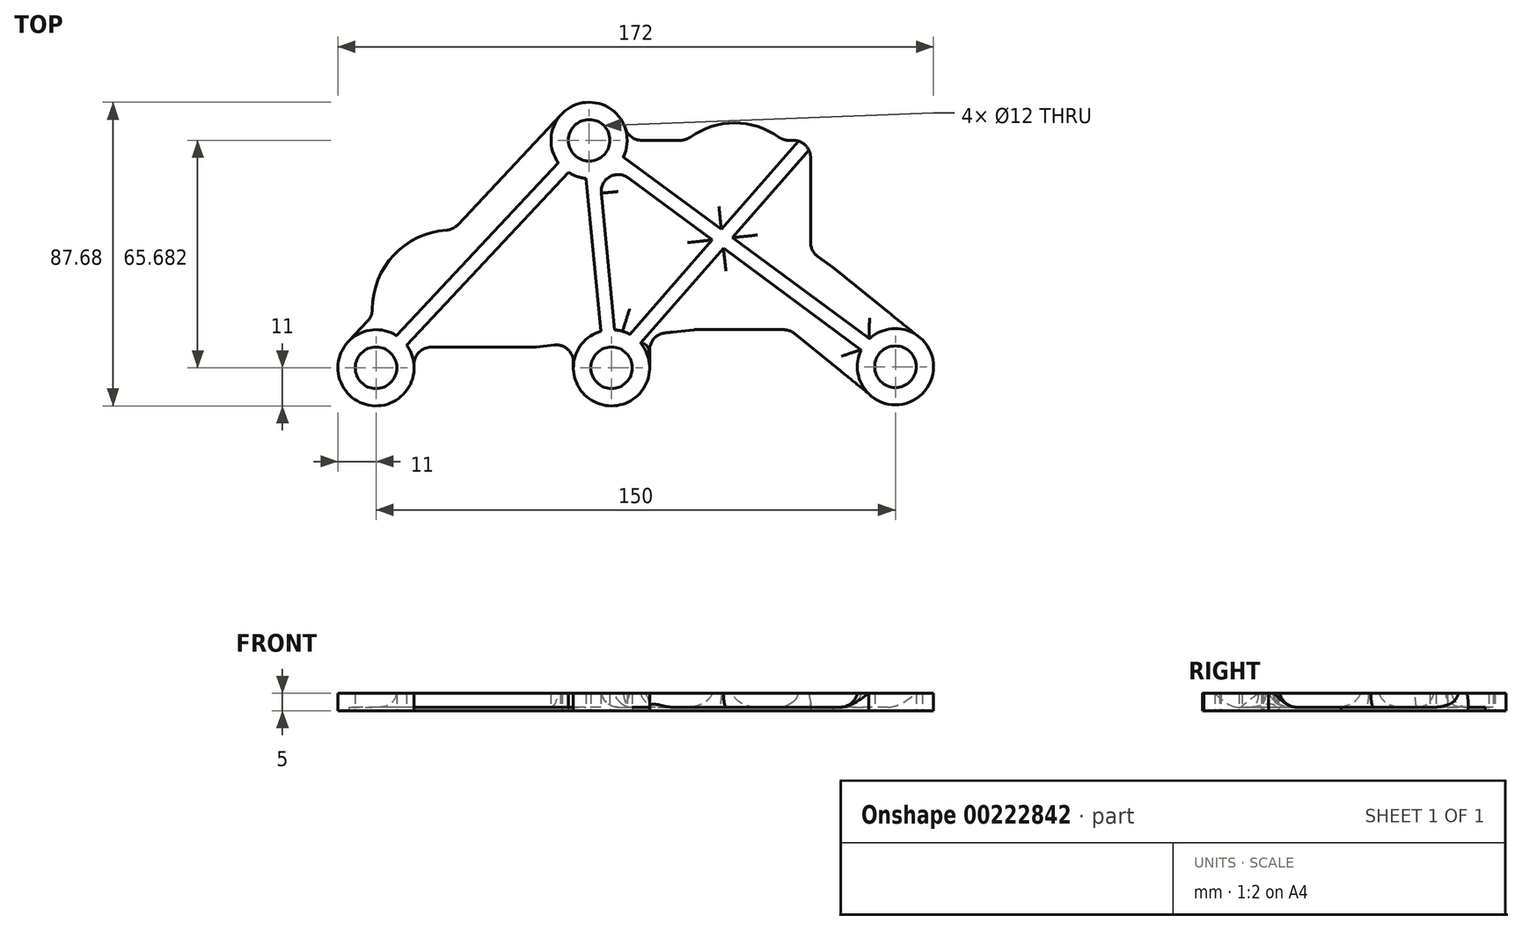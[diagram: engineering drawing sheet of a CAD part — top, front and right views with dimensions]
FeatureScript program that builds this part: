
annotation { "Feature Type Name" : "Feature", "Feature Type Description" : "" }
export const myFeature = defineFeature(function(context is Context, id is Id, definition is map)
    precondition{}
    {
        {
            var Q0;
            Q0=qCreatedBy(makeId("Top.planeOp"),FACE);
            var sketch = newSketch(context, id + "F0", { "sketchPlane" : qUnion([Q0])});
            skCircle(sketch, "E0", {"center": v(0, 0) * mm, "radius": 6 * mm});
            skCircle(sketch, "E1", {"center": v(-68, 0) * mm, "radius": 6 * mm});
            skCircle(sketch, "E2", {"center": v(-6.47, 65.68) * mm, "radius": 6 * mm});
            skArc(sketch, "E3", {"start": v(-75.78, 7.78) * mm, "mid": v(-72, -10.24) * mm, "end": v(-57, 0.43) * mm});
            skArc(sketch, "E4", {"start": v(-11, 0) * mm, "mid": v(0, -11) * mm, "end": v(11, 0) * mm});
            skArc(sketch, "E5", {"start": v(-14.25, 73.46) * mm, "mid": v(-14.5, 73.2) * mm, "end": v(-14.74, 72.94) * mm});
            skLineSegment(sketch, "E6", {"start": v(-68, 0) * mm, "end": v(-68, -11) * mm, "construction": true});
            skLineSegment(sketch, "E7", {"start": v(0, 0) * mm, "end": v(0, -11) * mm, "construction": true});
            skLineSegment(sketch, "E8", {"start": v(0, -11) * mm, "end": v(-68, -11) * mm, "construction": true});
            skLineSegment(sketch, "E9", {"start": v(0, -11) * mm, "end": v(48, -11) * mm, "construction": true});
            skLineSegment(sketch, "E10", {"start": v(48, -11) * mm, "end": v(-22, -11) * mm, "construction": true});
            skLineSegment(sketch, "E11", {"start": v(-22, -11) * mm, "end": v(-22, 6) * mm, "construction": true});
            skLineSegment(sketch, "E12", {"start": v(24, -11) * mm, "end": v(24, 11) * mm, "construction": true});
            skLineSegment(sketch, "E13", {"start": v(24.27, 11) * mm, "end": v(49.68, 11) * mm});
            skLineSegment(sketch, "E14", {"start": v(-6.47, 65.68) * mm, "end": v(1.3, 73.46) * mm, "construction": true});
            skLineSegment(sketch, "E15", {"start": v(-11, 0) * mm, "end": v(11, 0) * mm, "construction": true});
            skLineSegment(sketch, "E16", {"start": v(23.73, 10.97) * mm, "end": v(15.46, 10.07) * mm});
            skLineSegment(sketch, "E17.trimOffspring", {"start": v(-16.54, 6.6) * mm, "end": v(-21.73, 6.03) * mm});
            skLineSegment(sketch, "E18", {"start": v(-6.47, 65.68) * mm, "end": v(-14.25, 73.46) * mm, "construction": true});
            skLineSegment(sketch, "E19", {"start": v(-68, 0) * mm, "end": v(-75.78, 7.78) * mm, "construction": true});
            skLineSegment(sketch, "E20", {"start": v(-68, 0) * mm, "end": v(-79, 0) * mm, "construction": true});
            skLineSegment(sketch, "E21", {"start": v(-75.78, 7.78) * mm, "end": v(-70.43, 13.48) * mm});
            skLineSegment(sketch, "E22", {"start": v(-57, -0.43) * mm, "end": v(-57, 1) * mm});
            skLineSegment(sketch, "E23", {"start": v(-22.27, 6) * mm, "end": v(-52, 6) * mm});
            skPoint(sketch, "E24.orphan", {"position": v(-57, 12.43) * mm});
            skLineSegment(sketch, "E25", {"start": v(11, 0) * mm, "end": v(11, 5.1) * mm});
            skLineSegment(sketch, "E26", {"start": v(-11, 0) * mm, "end": v(-11, 1.62) * mm});
            skPoint(sketch, "E27", {"position": v(-69.01, 15) * mm});
            skPoint(sketch, "E28", {"position": v(-45.77, 39.81) * mm});
            skLineSegment(sketch, "E29", {"start": v(-62.63, 32.79) * mm, "end": v(-57.15, 27.66) * mm});
            skArc(sketch, "E30", {"start": v(-47.65, 39.76) * mm, "mid": v(-62.87, 32.54) * mm, "end": v(-69.08, 16.88) * mm});
            skPoint(sketch, "E31", {"position": v(52.5, 37.16) * mm});
            skPoint(sketch, "E32", {"position": v(25.66, 56.19) * mm});
            skLineSegment(sketch, "E33", {"start": v(52.8, 73.14) * mm, "end": v(52.5, 73.16) * mm});
            skLineSegment(sketch, "E34.trimOffspring", {"start": v(59.6, 32.11) * mm, "end": v(64, 29) * mm});
            skPoint(sketch, "E35", {"position": v(82, 0.31) * mm});
            skCircle(sketch, "E36", {"center": v(82, 0.31) * mm, "radius": 6 * mm});
            skArc(sketch, "E37", {"start": v(74.22, -7.46) * mm, "mid": v(90.54, -6.61) * mm, "end": v(88, 9.53) * mm});
            skLineSegment(sketch, "E38", {"start": v(82, 0.31) * mm, "end": v(93, 0.31) * mm, "construction": true});
            skLineSegment(sketch, "E39", {"start": v(93, 0.31) * mm, "end": v(82, 0.31) * mm, "construction": true});
            skLineSegment(sketch, "E40", {"start": v(82, 0.31) * mm, "end": v(89.78, 8.1) * mm, "construction": true});
            skLineSegment(sketch, "E41", {"start": v(89.78, 8.1) * mm, "end": v(64, 29) * mm});
            skLineSegment(sketch, "E42", {"start": v(74.22, -7.46) * mm, "end": v(82, 0.31) * mm, "construction": true});
            skLineSegment(sketch, "E43", {"start": v(74.22, -7.46) * mm, "end": v(52.83, 9.88) * mm});
            skLineSegment(sketch, "E44.trimOffspring", {"start": v(-44.35, 41.33) * mm, "end": v(-14.25, 73.46) * mm});
            skPoint(sketch, "E45.visualSharp", {"position": v(-57, 6) * mm});
            skArc(sketch, "E45.filletArc", {"start": v(-52, 6) * mm, "mid": v(-55.54, 4.54) * mm, "end": v(-57, 1) * mm});
            skPoint(sketch, "E46.visualSharp", {"position": v(-22, 6) * mm});
            skArc(sketch, "E46.filletArc", {"start": v(-22.27, 6) * mm, "mid": v(-22, 6) * mm, "end": v(-21.73, 6.03) * mm});
            skArc(sketch, "E47.filletArc", {"start": v(-70.43, 13.48) * mm, "mid": v(-69.44, 15.05) * mm, "end": v(-69.08, 16.88) * mm});
            skArc(sketch, "E48.filletArc", {"start": v(-47.65, 39.76) * mm, "mid": v(-45.85, 40.23) * mm, "end": v(-44.35, 41.33) * mm});
            skPoint(sketch, "E49.visualSharp", {"position": v(-11, 7.2) * mm});
            skArc(sketch, "E49.filletArc", {"start": v(-11, 1.62) * mm, "mid": v(-12.66, 5.34) * mm, "end": v(-16.54, 6.6) * mm});
            skPoint(sketch, "E50.visualSharp", {"position": v(11, 9.59) * mm});
            skArc(sketch, "E50.filletArc", {"start": v(15.46, 10.07) * mm, "mid": v(12.28, 8.44) * mm, "end": v(11, 5.1) * mm});
            skPoint(sketch, "E51.visualSharp", {"position": v(24, 11) * mm});
            skArc(sketch, "E51.filletArc", {"start": v(24.27, 11) * mm, "mid": v(24, 11) * mm, "end": v(23.73, 10.97) * mm});
            skPoint(sketch, "E52.visualSharp", {"position": v(51.46, 11) * mm});
            skArc(sketch, "E52.filletArc", {"start": v(52.83, 9.88) * mm, "mid": v(51.35, 10.71) * mm, "end": v(49.68, 11) * mm});
            skPoint(sketch, "E53.visualSharp", {"position": v(52.5, 73.16) * mm});
            skLineSegment(sketch, "E54", {"start": v(57.5, 60.68) * mm, "end": v(57.5, 36.2) * mm});
            skPoint(sketch, "E55.visualSharp", {"position": v(57.5, 33.6) * mm});
            skArc(sketch, "E55.filletArc", {"start": v(57.5, 36.2) * mm, "mid": v(58.06, 33.9) * mm, "end": v(59.6, 32.11) * mm});
            skLineSegment(sketch, "E56.trimOffspring", {"start": v(4.53, 65.68) * mm, "end": v(12.3, 65.68) * mm, "construction": true});
            skLineSegment(sketch, "E57.trimOffspring", {"start": v(8.73, 65.68) * mm, "end": v(19.85, 65.68) * mm});
            skLineSegment(sketch, "E58", {"start": v(-68, 0) * mm, "end": v(-63.9, 4.38) * mm, "construction": true});
            skLineSegment(sketch, "E59.trimOffspring", {"start": v(-14, 57.65) * mm, "end": v(-6.47, 65.68) * mm, "construction": true});
            skArc(sketch, "E60.trimOffspring", {"start": v(3.98, 69.12) * mm, "mid": v(-4.27, 76.46) * mm, "end": v(-14.74, 72.94) * mm});
            skPoint(sketch, "E61.visualSharp", {"position": v(57.5, 65.68) * mm});
            skArc(sketch, "E61.filletArc", {"start": v(57.5, 60.68) * mm, "mid": v(56.04, 64.22) * mm, "end": v(52.5, 65.68) * mm});
            skPoint(sketch, "E62", {"position": v(21.53, 65.68) * mm});
            skPoint(sketch, "E63", {"position": v(49.53, 65.68) * mm});
            skPoint(sketch, "E64", {"position": v(35.53, 65.68) * mm});
            skArc(sketch, "E65", {"start": v(48.32, 66.6) * mm, "mid": v(35.53, 70.68) * mm, "end": v(22.74, 66.6) * mm});
            skLineSegment(sketch, "E66.trimOffspring", {"start": v(51.21, 65.68) * mm, "end": v(52.5, 65.68) * mm});
            skPoint(sketch, "E67.start.orphan", {"position": v(35.53, 70.68) * mm});
            skPoint(sketch, "E68.visualSharp", {"position": v(4.53, 65.68) * mm});
            skArc(sketch, "E68.filletArc", {"start": v(3.98, 69.12) * mm, "mid": v(5.8, 66.63) * mm, "end": v(8.73, 65.68) * mm});
            skArc(sketch, "E69.filletArc", {"start": v(19.85, 65.68) * mm, "mid": v(21.36, 65.92) * mm, "end": v(22.74, 66.6) * mm});
            skArc(sketch, "E70.filletArc", {"start": v(48.32, 66.6) * mm, "mid": v(49.7, 65.92) * mm, "end": v(51.21, 65.68) * mm});
            skSolve(sketch);
        }
        {
            var Q0;
            Q0=makeQuery(id+"F0.imprint","IMPRINT",FACE,{"disambiguationData":[TD([[makeQuery(id+"F0.imprint","IMPRINT",EDGE,{"derivedFrom":sQuery(id+"F0.wireOp",EDGE,"E13")}),1.0]])]});
            extrude(context, id + "F1", {"entities" : qUnion([Q0]), "depth" : 1 * mm});
        }
        {
            var Q0;
            Q0=makeQuery(id+"F1.opExtrude","CAP_FACE",FACE,{"disambiguationData":[OSD([sQuery(id+"F0.wireOp",EDGE,"E0"),sQuery(id+"F0.wireOp",EDGE,"E1"),sQuery(id+"F0.wireOp",EDGE,"E2"),sQuery(id+"F0.wireOp",EDGE,"E3"),sQuery(id+"F0.wireOp",EDGE,"E4"),sQuery(id+"F0.wireOp",EDGE,"E5"),sQuery(id+"F0.wireOp",EDGE,"E13"),sQuery(id+"F0.wireOp",EDGE,"E16"),sQuery(id+"F0.wireOp",EDGE,"E17.trimOffspring"),sQuery(id+"F0.wireOp",EDGE,"E21"),sQuery(id+"F0.wireOp",EDGE,"E22"),sQuery(id+"F0.wireOp",EDGE,"E23"),sQuery(id+"F0.wireOp",EDGE,"E25"),sQuery(id+"F0.wireOp",EDGE,"E26"),sQuery(id+"F0.wireOp",EDGE,"E30"),sQuery(id+"F0.wireOp",EDGE,"3UzAlsw2-RzgX-fS7Z-g7R3-vtdSIq3O0E33"),sQuery(id+"F0.wireOp",EDGE,"E33"),sQuery(id+"F0.wireOp",EDGE,"E34.trimOffspring"),sQuery(id+"F0.wireOp",EDGE,"E36"),sQuery(id+"F0.wireOp",EDGE,"E37"),sQuery(id+"F0.wireOp",EDGE,"E41"),sQuery(id+"F0.wireOp",EDGE,"E43"),sQuery(id+"F0.wireOp",EDGE,"E44.trimOffspring")])],"isStart":false});
            var sketch = newSketch(context, id + "F2", { "sketchPlane" : qUnion([Q0])});
            skLineSegment(sketch, "E71", {"start": v(-5.81, 76.66) * mm, "end": v(-6.47, 65.68) * mm, "construction": true});
            skLineSegment(sketch, "E72", {"start": v(-5.4, 54.74) * mm, "end": v(-6.47, 65.68) * mm, "construction": true});
            skPoint(sketch, "E73.orphan", {"position": v(-68, 0) * mm});
            skLineSegment(sketch, "E74", {"start": v(-68, 0) * mm, "end": v(-27.66, 43.06) * mm, "construction": true});
            skArc(sketch, "E75", {"start": v(-62.06, 9.26) * mm, "mid": v(-75.52, -8.03) * mm, "end": v(-59.15, 6.53) * mm});
            skLineSegment(sketch, "E76", {"start": v(-12.4, 56.42) * mm, "end": v(-59.15, 6.53) * mm});
            skLineSegment(sketch, "E77", {"start": v(-62.06, 9.26) * mm, "end": v(-15.33, 59.16) * mm});
            skLineSegment(sketch, "E78", {"start": v(-57, 1) * mm, "end": v(-67.68, 11) * mm, "construction": true});
            skPoint(sketch, "E79", {"position": v(-46.8, 22.62) * mm});
            skPoint(sketch, "E80", {"position": v(-27.66, 43.06) * mm});
            skPoint(sketch, "E81.startDerivative.orphan", {"position": v(-72.76, 11) * mm});
            skLineSegment(sketch, "E82.trimOffspring", {"start": v(-14, 57.65) * mm, "end": v(-6.47, 65.68) * mm, "construction": true});
            skLineSegment(sketch, "E83", {"start": v(0.93, 10.96) * mm, "end": v(-3.42, 55.11) * mm});
            skLineSegment(sketch, "E84", {"start": v(-3.05, 10.57) * mm, "end": v(-7.4, 54.72) * mm});
            skLineSegment(sketch, "E85", {"start": v(-6.47, 65.68) * mm, "end": v(-5.1, 67.14) * mm, "construction": true});
            skPoint(sketch, "E86.orphan", {"position": v(83.19, 1.92) * mm});
            skPoint(sketch, "E87.orphan", {"position": v(51.14, 71.88) * mm});
            skCircle(sketch, "E88.converted", {"center": v(82, 0.31) * mm, "radius": 11 * mm});
            skArc(sketch, "E89", {"start": v(-12.4, 56.42) * mm, "mid": v(-10, 55.27) * mm, "end": v(-7.4, 54.72) * mm});
            skArc(sketch, "E90.trimOffspring", {"start": v(-3.42, 55.11) * mm, "mid": v(-2.93, 76.1) * mm, "end": v(-15.33, 59.16) * mm});
            skArc(sketch, "E91", {"start": v(5.28, 9.65) * mm, "mid": v(3.17, 10.53) * mm, "end": v(0.93, 10.96) * mm});
            skLineSegment(sketch, "E92", {"start": v(-6.47, 65.68) * mm, "end": v(82, 0.31) * mm, "construction": true});
            skLineSegment(sketch, "E93", {"start": v(72.11, 5.13) * mm, "end": v(32.31, 34.54) * mm});
            skLineSegment(sketch, "E94", {"start": v(74.49, 8.35) * mm, "end": v(34.95, 37.56) * mm});
            skLineSegment(sketch, "E95.trimOffspring", {"start": v(31.72, 39.95) * mm, "end": v(3.42, 60.86) * mm});
            skLineSegment(sketch, "E96.trimOffspring", {"start": v(29.08, 36.93) * mm, "end": v(1.04, 57.65) * mm});
            skPoint(sketch, "E97.end.orphan", {"position": v(30.24, 38.56) * mm});
            skLineSegment(sketch, "E98", {"start": v(8.39, 7.12) * mm, "end": v(32.31, 34.54) * mm});
            skLineSegment(sketch, "E99", {"start": v(5.28, 9.65) * mm, "end": v(29.08, 36.93) * mm});
            skArc(sketch, "E100.trimOffspring", {"start": v(-3.05, 10.57) * mm, "mid": v(-3.18, -10.53) * mm, "end": v(8.39, 7.12) * mm});
            skLineSegment(sketch, "E101.trimOffspring", {"start": v(31.72, 39.95) * mm, "end": v(53.98, 65.46) * mm});
            skLineSegment(sketch, "E102.trimOffspring", {"start": v(34.95, 37.56) * mm, "end": v(57, 62.84) * mm});
            skArc(sketch, "E103", {"start": v(57, 62.84) * mm, "mid": v(55.77, 64.47) * mm, "end": v(53.98, 65.46) * mm});
            skSolve(sketch);
        }
        {
            var Q0;
            Q0=makeQuery(id+"F2.imprint","IMPRINT",FACE,{"disambiguationData":[TD([[makeQuery(id+"F2.imprint","IMPRINT",EDGE,{"derivedFrom":makeQuery(id+"F1.opExtrude","CAP_EDGE",EDGE,{"disambiguationData":[OSD([sQuery(id+"F0.wireOp",EDGE,"E2")])],"isStart":false})}),-1.0]])]});
            var Q1;
            Q1=makeQuery(id+"F2.imprint","IMPRINT",FACE,{"disambiguationData":[TD([[makeQuery(id+"F2.imprint","IMPRINT",EDGE,{"derivedFrom":makeQuery(id+"F1.opExtrude","CAP_EDGE",EDGE,{"disambiguationData":[OSD([sQuery(id+"F0.wireOp",EDGE,"E0")])],"isStart":false})}),-1.0]])]});
            var Q2;
            Q2=makeQuery(id+"F2.imprint","IMPRINT",FACE,{"disambiguationData":[TD([[makeQuery(id+"F2.imprint","IMPRINT",EDGE,{"derivedFrom":makeQuery(id+"F1.opExtrude","CAP_EDGE",EDGE,{"disambiguationData":[OSD([sQuery(id+"F0.wireOp",EDGE,"E1")])],"isStart":false})}),-1.0]])]});
            var Q3;
            {var subQ2=sQuery(id+"F2.wireOp",EDGE,"E76");Q3=makeQuery(id+"F2.imprint","IMPRINT",FACE,{"disambiguationData":[TD([[makeQuery(id+"F2.imprint","IMPRINT",EDGE,{"derivedFrom":subQ2}),-1.0]])]});}
            var Q4;
            Q4=makeQuery(id+"F2.imprint","IMPRINT",FACE,{"disambiguationData":[TD([[makeQuery(id+"F2.imprint","IMPRINT",EDGE,{"derivedFrom":makeQuery(id+"F1.opExtrude","CAP_EDGE",EDGE,{"disambiguationData":[OSD([sQuery(id+"F0.wireOp",EDGE,"E36")])],"isStart":false})}),-1.0]])]});
            extrude(context, id + "F3", {"entities" : qUnion([Q0, Q1, Q2, Q3, Q4]), "operationType" : NewBodyOperationType.ADD, "depth" : 4 * mm});
        }
        {
            var Q0;
            Q0=makeQuery(id+"F3.opExtrude","CAP_EDGE",EDGE,{"disambiguationData":[OSD([sQuery(id+"F2.wireOp",EDGE,"E76")])],"isStart":true});
            var Q1;
            Q1=makeQuery(id+"F3.opExtrude","CAP_EDGE",EDGE,{"disambiguationData":[OSD([sQuery(id+"F2.wireOp",EDGE,"E83")])],"isStart":true});
            var Q2;
            Q2=makeQuery(id+"F3.opExtrude","CAP_EDGE",EDGE,{"disambiguationData":[OSD([sQuery(id+"F2.wireOp",EDGE,"E98")])],"isStart":true});
            var Q3;
            Q3=makeQuery(id+"F3.opExtrude","CAP_EDGE",EDGE,{"disambiguationData":[OSD([sQuery(id+"F2.wireOp",EDGE,"E77")])],"isStart":true});
            var Q4;
            Q4=makeQuery(id+"F3.opExtrude","CAP_EDGE",EDGE,{"disambiguationData":[OSD([sQuery(id+"F2.wireOp",EDGE,"E99")])],"isStart":true});
            var Q5;
            Q5=makeQuery(id+"F3.opExtrude","CAP_EDGE",EDGE,{"disambiguationData":[OSD([sQuery(id+"F2.wireOp",EDGE,"E84")])],"isStart":true});
            fillet(context, id + "F4", {"entities" : qUnion([Q0, Q1, Q2, Q3, Q4, Q5]), "radius" : 5 * mm, "tangentPropagation" : true, "allowEdgeOverflow" : false});
        }
        {
            var Q0;
            Q0=makeQuery(id+"F3.opExtrude","CAP_EDGE",EDGE,{"disambiguationData":[OSD([sQuery(id+"F2.wireOp",EDGE,"E96.trimOffspring")])],"isStart":true});
            var Q1;
            Q1=makeQuery(id+"F3.opExtrude","CAP_EDGE",EDGE,{"disambiguationData":[OSD([sQuery(id+"F2.wireOp",EDGE,"E93")])],"isStart":true});
            var Q2;
            Q2=makeQuery(id+"F3.opExtrude","CAP_EDGE",EDGE,{"disambiguationData":[OSD([sQuery(id+"F2.wireOp",EDGE,"E95.trimOffspring")])],"isStart":true});
            var Q3;
            Q3=makeQuery(id+"F3.opExtrude","CAP_EDGE",EDGE,{"disambiguationData":[OSD([sQuery(id+"F2.wireOp",EDGE,"E94")])],"isStart":true});
            var Q4;
            {var subQ0=sQuery(id+"F0.wireOp",EDGE,"E26");var subQ2=sQuery(id+"F2.wireOp",EDGE,"E100.trimOffspring");Q4=makeQuery(id+"F3.boolean.opBoolean","SPLIT",EDGE,{"disambiguationData":[TD([makeQuery(id+"F1.opExtrude","SWEPT_FACE",FACE,{"disambiguationData":[OSD([subQ0])]})])],"derivedFrom":makeQuery(id+"F3.opExtrude","CAP_EDGE",EDGE,{"disambiguationData":[OSD([subQ2])],"isStart":true})});}
            var Q5;
            {var subQ0=sQuery(id+"F2.wireOp",EDGE,"E88.converted");Q5=makeQuery(id+"F3.opExtrude","CAP_EDGE",EDGE,{"disambiguationData":[OSD([subQ0]),TDD([makeQuery(id+"F2.imprint","IMPRINT",EDGE,{"disambiguationData":[TD([[makeQuery(id+"F2.imprint","INTERSECT",VERTEX,{"derivedFrom":[subQ0,sQuery(id+"F2.wireOp",EDGE,"E94")]}),1.0]])],"derivedFrom":subQ0})])],"isStart":true});}
            var Q6;
            {var subQ0=sQuery(id+"F2.wireOp",EDGE,"E88.converted");var subQ1=makeQuery(id+"F2.imprint","INTERSECT",VERTEX,{"derivedFrom":[makeQuery(id+"F1.opExtrude","CAP_EDGE",EDGE,{"disambiguationData":[OSD([sQuery(id+"F0.wireOp",EDGE,"E43")])],"isStart":false}),subQ0]});Q6=makeQuery(id+"F3.opExtrude","CAP_EDGE",EDGE,{"disambiguationData":[OSD([subQ0]),TDD([makeQuery(id+"F2.imprint","IMPRINT",EDGE,{"disambiguationData":[TD([[subQ1,-1.0]])],"derivedFrom":subQ0}),makeQuery(id+"F2.imprint","IMPRINT",EDGE,{"disambiguationData":[TD([[subQ1,1.0]])],"derivedFrom":subQ0})])],"isStart":true});}
            var Q7;
            Q7=makeQuery(id+"F3.opExtrude","CAP_EDGE",EDGE,{"disambiguationData":[OSD([sQuery(id+"F2.wireOp",EDGE,"E101.trimOffspring")])],"isStart":true});
            var Q8;
            Q8=makeQuery(id+"F3.opExtrude","CAP_EDGE",EDGE,{"disambiguationData":[OSD([sQuery(id+"F2.wireOp",EDGE,"E102.trimOffspring")])],"isStart":true});
            fillet(context, id + "F5", {"entities" : qUnion([Q0, Q1, Q2, Q3, Q4, Q5, Q6, Q7, Q8]), "radius" : 5 * mm, "tangentPropagation" : true, "allowEdgeOverflow" : false});
        }
    });
